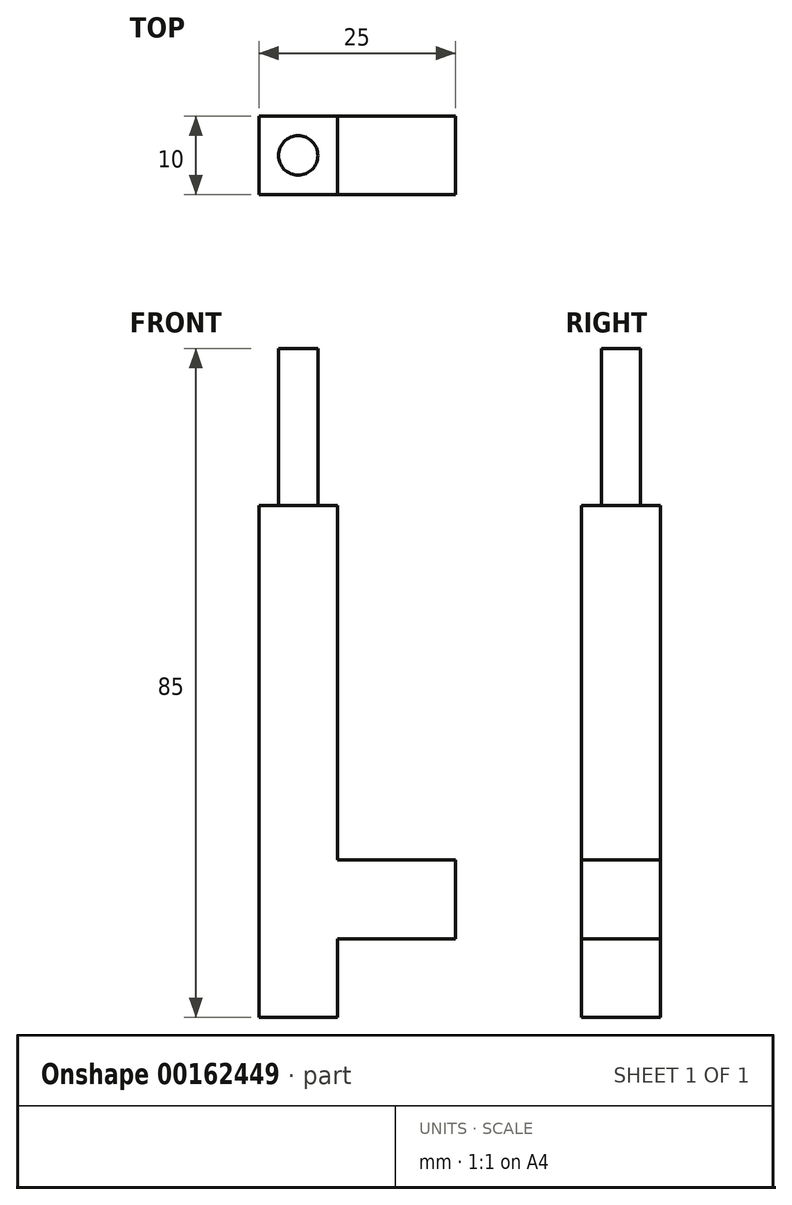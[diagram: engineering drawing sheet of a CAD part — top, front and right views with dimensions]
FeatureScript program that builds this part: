
annotation { "Feature Type Name" : "Feature", "Feature Type Description" : "" }
export const myFeature = defineFeature(function(context is Context, id is Id, definition is map)
    precondition{}
    {
        {
            var Q0;
            Q0=qCreatedBy(makeId("Front.planeOp"),FACE);
            var sketch = newSketch(context, id + "F0", { "sketchPlane" : qUnion([Q0])});
            skLineSegment(sketch, "E0.bottom", {"start": v(5, -32.5) * mm, "end": v(-5, -32.5) * mm});
            skLineSegment(sketch, "E0.top", {"start": v(5, 32.5) * mm, "end": v(-5, 32.5) * mm});
            skLineSegment(sketch, "E0.left", {"start": v(5, -32.5) * mm, "end": v(5, -22.5) * mm});
            skLineSegment(sketch, "E0.right", {"start": v(-5, -32.5) * mm, "end": v(-5, 32.5) * mm});
            skPoint(sketch, "E0.middle", {"position": v(0, 0) * mm});
            skPoint(sketch, "E1", {"position": v(5, -22.5) * mm});
            skLineSegment(sketch, "E2.bottom", {"start": v(5, -22.5) * mm, "end": v(20, -22.5) * mm});
            skLineSegment(sketch, "E2.top", {"start": v(5, -12.5) * mm, "end": v(20, -12.5) * mm});
            skLineSegment(sketch, "E2.right", {"start": v(20, -22.5) * mm, "end": v(20, -12.5) * mm});
            skLineSegment(sketch, "E3.trimOffspring", {"start": v(5, -12.5) * mm, "end": v(5, 32.5) * mm});
            skSolve(sketch);
        }
        {
            var Q0;
            Q0 = qSketchRegion(id + "F0", true);
            extrude(context, id + "F1", {"entities" : qUnion([Q0]), "depth" : 10 * mm});
        }
        {
            var Q0;
            Q0=makeQuery(id+"F1.opExtrude","SWEPT_FACE",FACE,{"disambiguationData":[OSD([sQuery(id+"F0.wireOp",EDGE,"E0.top")])]});
            var sketch = newSketch(context, id + "F2", { "sketchPlane" : qUnion([Q0])});
            skLineSegment(sketch, "E4", {"start": v(5, 0) * mm, "end": v(5, -5) * mm});
            skLineSegment(sketch, "E5", {"start": v(5, -10) * mm, "end": v(0, -10) * mm});
            skCircle(sketch, "E6", {"center": v(0, -5) * mm, "radius": 2.5 * mm});
            skSolve(sketch);
        }
        {
            var Q0;
            Q0=makeQuery(id+"F2.imprint","IMPRINT",FACE,{"disambiguationData":[TD([[makeQuery(id+"F2.imprint","IMPRINT",EDGE,{"derivedFrom":sQuery(id+"F2.wireOp",EDGE,"E6")}),1.0]])]});
            extrude(context, id + "F3", {"entities" : qUnion([Q0]), "operationType" : NewBodyOperationType.ADD, "depth" : 20 * mm});
        }
    });
